# Revit family: QF_T&S_B-0133-LB
name_source: partatom
category: Specialty Equipment
revit_build: Autodesk Revit 2015 (Build: 20140606_1530(x64)
units: mm (PartAtom-declared; Revit-internal decimal feet)

## types (1)
- By Type
    Cold Water Connection Height = 0"
    Cold Water Inlet Flow = 1.420 GPM
    Cold Water Maximum Pressure = 125.00 psi
    Cold Water Minimum Pressure = 20.00 psi
    Cold Water Size = 0"
    Connector 1 Description = Cold Water Inlet
    Connector 2 Description = Hot Water Inlet
    Description = B-0133 Pre-Rinse Unit Less Base Faucet (-LB)
    Faucet Material = <By Category>
    Foodservice Equipment Identifier = Yes
    Hot Water Connection Height = 0"
    Hot Water Consumption = 1.420 GPM
    Hot Water Inlet Flow = 1.420 GPM
    Hot Water Maximum Pressure = 125.00 psi
    Hot Water Minimum Pressure = 20.00 psi
    Hot Water Size = 0"
    Identify Quantity as Lot = Yes
    Keynote = ﻿﻿               ﻿      ﻿​ ​﻿​ ﻿                         ﻿   ​                  ﻿ ​    ﻿   ​ ​   ​     ﻿  ﻿﻿   ﻿﻿ ﻿                                        ​           ﻿﻿﻿   ﻿  ﻿          ​                   ​​ ﻿                                           ﻿ ﻿                   ​ ﻿                  ﻿        ﻿           ﻿                       ​     ﻿           ﻿﻿
    Manufacturer = T&S Brass and Bronze Works, Inc.
    Manufacturer Fax = 1-800-868-0084
    Model = B-0133-LB
    Plumbing Remarks = Pressure: 20 - 125 psi, Temperature: 40 F - 140 F, Flow Rate: 1.42 GPM @ 60 psi
    Product Documentation Link = http://catalog.tsbrass.com
    Type Comments = ﻿﻿              
http://www.tsbrass.com ﻿      ﻿​ ​﻿​ ﻿                         ﻿   ​                  ﻿ ​    ﻿   ​ ​   ​     ﻿  ﻿﻿   ﻿﻿ ﻿                                        ​           ﻿﻿﻿   ﻿  ﻿          ​                   ​​ ﻿                                           ﻿ ﻿                   ​ ﻿                  ﻿        ﻿           ﻿                       ​     ﻿           ﻿﻿
    URL = http://www.tsbrass.com
    Water Supply Radius = 3/16"
    Weight in Pounds = 0

## geometry (parser evidence)
native form markers: Blend x4, Sweep x2
no freeform markers — native parametric forms only
